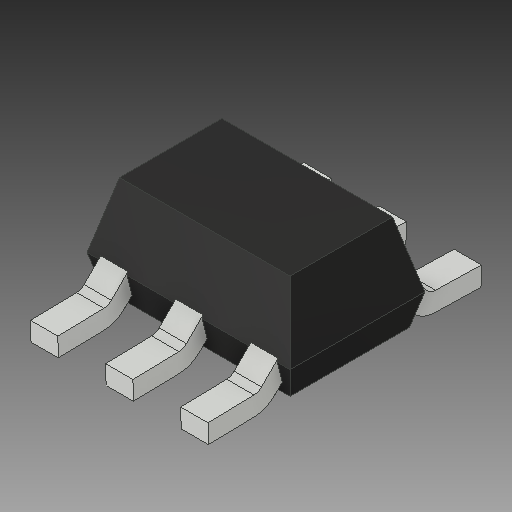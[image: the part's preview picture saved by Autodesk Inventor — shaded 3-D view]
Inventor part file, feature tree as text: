
AUTODESK INVENTOR PART (.ipt)
format: ipt  version: 2019 (Build 230136000, 136)  size: 139,776 bytes
history: mixed  units: in
note: dims shown in document units (in); Inventor stores cm internally (conversion verified against a paired STEP export)
features: mirror x1, imported_body x1
ambient origin geometry x8: Origin, YZ Plane, XZ Plane, XY Plane, X Axis, Y Axis, Z Axis, Center Point
bodies: Solid1 (imported_parasolid)
feature tree (2):
  mirror  "Mirror1"
  imported_body  NMx_Import_Brep_tag  [imported B-rep: ~64 faces, bbox_mm=[2.975, 1.489961, 4.006585]]
